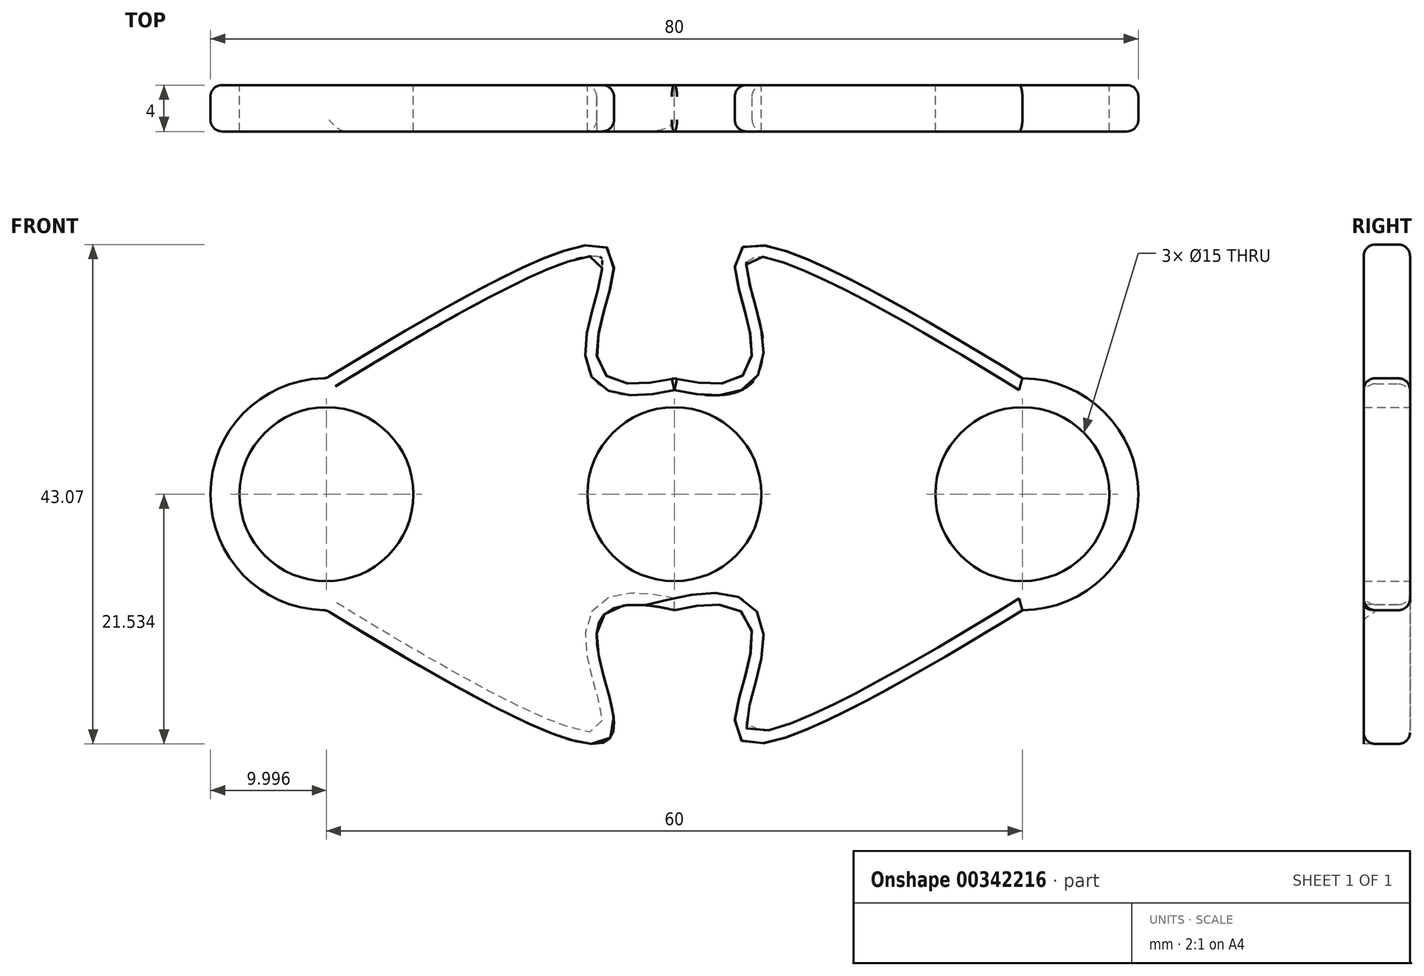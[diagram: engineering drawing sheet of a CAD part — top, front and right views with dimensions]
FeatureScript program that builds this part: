
annotation { "Feature Type Name" : "Feature", "Feature Type Description" : "" }
export const myFeature = defineFeature(function(context is Context, id is Id, definition is map)
    precondition{}
    {
        {
            var Q0;
            Q0=qCreatedBy(makeId("Front.planeOp"),FACE);
            var sketch = newSketch(context, id + "F0", { "sketchPlane" : qUnion([Q0])});
            skLineSegment(sketch, "E0.left", {"start": v(-32.53, 13.05) * mm, "end": v(-32.53, 13.05) * mm});
            skLineSegment(sketch, "E0.right", {"start": v(47.47, 13.05) * mm, "end": v(47.47, 13.05) * mm});
            skLineSegment(sketch, "E1", {"start": v(7.47, 23.05) * mm, "end": v(7.47, 3.05) * mm, "construction": true});
            skCircle(sketch, "E2", {"center": v(7.47, 13.05) * mm, "radius": 7.5 * mm});
            skLineSegment(sketch, "E3", {"start": v(27.47, 23.05) * mm, "end": v(27.47, 3.05) * mm, "construction": true});
            skLineSegment(sketch, "E4.MirrorCS", {"start": v(-12.53, 23.05) * mm, "end": v(-12.53, 3.05) * mm, "construction": true});
            skLineSegment(sketch, "E5", {"start": v(-32.53, 13.05) * mm, "end": v(47.47, 13.05) * mm, "construction": true});
            skCircle(sketch, "E6", {"center": v(37.47, 13.05) * mm, "radius": 7.5 * mm});
            skCircle(sketch, "E7.MirrorC", {"center": v(-22.53, 13.05) * mm, "radius": 7.5 * mm});
            skPoint(sketch, "E8.visualSharp", {"position": v(-32.53, 23.05) * mm});
            skArc(sketch, "E8.filletArc", {"start": v(-22.53, 23.05) * mm, "mid": v(-29.6, 20.13) * mm, "end": v(-32.53, 13.05) * mm});
            skPoint(sketch, "E9.visualSharp", {"position": v(-32.53, 3.05) * mm});
            skArc(sketch, "E9.filletArc", {"start": v(-32.53, 13.05) * mm, "mid": v(-29.6, 5.98) * mm, "end": v(-22.53, 3.05) * mm});
            skPoint(sketch, "E10.visualSharp", {"position": v(47.47, 23.05) * mm});
            skArc(sketch, "E10.filletArc", {"start": v(47.47, 13.05) * mm, "mid": v(44.54, 20.13) * mm, "end": v(37.47, 23.05) * mm});
            skPoint(sketch, "E11.visualSharp", {"position": v(47.47, 3.05) * mm});
            skArc(sketch, "E11.filletArc", {"start": v(37.47, 3.05) * mm, "mid": v(44.54, 5.98) * mm, "end": v(47.47, 13.05) * mm});
            skFitSpline(sketch, "E12", {"points": [v(-22.53, 23.05) * mm, v(7.47, 23.05) * mm], "startDerivative": vector(137.5, 84.56) * mm, "endDerivative": vector(60, 14.29) * mm});
            skFitSpline(sketch, "E13.MirrorCS", {"points": [v(37.47, 23.05) * mm, v(7.47, 23.05) * mm], "startDerivative": vector(-137.5, 84.56) * mm, "endDerivative": vector(-60, 14.29) * mm});
            skFitSpline(sketch, "E14.MirrorCS", {"points": [v(-22.53, 3.05) * mm, v(7.47, 3.05) * mm], "startDerivative": vector(137.5, -84.56) * mm, "endDerivative": vector(60, -14.29) * mm});
            skFitSpline(sketch, "E15.MirrorCS", {"points": [v(37.47, 3.05) * mm, v(7.47, 3.05) * mm], "startDerivative": vector(-137.5, -84.56) * mm, "endDerivative": vector(-60, -14.29) * mm});
            skSolve(sketch);
        }
        {
            var Q0;
            Q0=makeQuery(id+"F0.imprint","IMPRINT",FACE,{"disambiguationData":[TD([[makeQuery(id+"F0.imprint","IMPRINT",EDGE,{"derivedFrom":sQuery(id+"F0.wireOp",EDGE,"E2")}),-1.0]])]});
            extrude(context, id + "F1", {"entities" : qUnion([Q0]), "depth" : 4 * mm});
        }
        {
            var Q0;
            Q0=makeQuery(id+"F1.opExtrude","CAP_EDGE",EDGE,{"disambiguationData":[OSD([sQuery(id+"F0.wireOp",EDGE,"E12")])],"isStart":false});
            var Q1;
            Q1=makeQuery(id+"F1.opExtrude","CAP_EDGE",EDGE,{"disambiguationData":[OSD([sQuery(id+"F0.wireOp",EDGE,"E13.MirrorCS")])],"isStart":false});
            var Q2;
            Q2=makeQuery(id+"F1.opExtrude","CAP_EDGE",EDGE,{"disambiguationData":[OSD([sQuery(id+"F0.wireOp",EDGE,"E15.MirrorCS")])],"isStart":true});
            var Q3;
            Q3=makeQuery(id+"F1.opExtrude","CAP_EDGE",EDGE,{"disambiguationData":[OSD([sQuery(id+"F0.wireOp",EDGE,"E14.MirrorCS")])],"isStart":true});
            var Q4;
            Q4=makeQuery(id+"F1.opExtrude","CAP_EDGE",EDGE,{"disambiguationData":[OSD([sQuery(id+"F0.wireOp",EDGE,"E12")])],"isStart":true});
            var Q5;
            Q5=makeQuery(id+"F1.opExtrude","CAP_EDGE",EDGE,{"disambiguationData":[OSD([sQuery(id+"F0.wireOp",EDGE,"E8.filletArc"),sQuery(id+"F0.wireOp",EDGE,"E9.filletArc")])],"isStart":true});
            var Q6;
            Q6=makeQuery(id+"F1.opExtrude","SWEPT_FACE",FACE,{"disambiguationData":[OSD([sQuery(id+"F0.wireOp",EDGE,"E8.filletArc"),sQuery(id+"F0.wireOp",EDGE,"E9.filletArc")])]});
            var Q7;
            Q7=makeQuery(id+"F1.opExtrude","CAP_EDGE",EDGE,{"disambiguationData":[OSD([sQuery(id+"F0.wireOp",EDGE,"E13.MirrorCS")])],"isStart":true});
            var Q8;
            Q8=makeQuery(id+"F1.opExtrude","CAP_EDGE",EDGE,{"disambiguationData":[OSD([sQuery(id+"F0.wireOp",EDGE,"E10.filletArc"),sQuery(id+"F0.wireOp",EDGE,"E11.filletArc")])],"isStart":true});
            var Q9;
            Q9=makeQuery(id+"F1.opExtrude","CAP_EDGE",EDGE,{"disambiguationData":[OSD([sQuery(id+"F0.wireOp",EDGE,"E10.filletArc"),sQuery(id+"F0.wireOp",EDGE,"E11.filletArc")])],"isStart":false});
            var Q10;
            Q10=makeQuery(id+"F1.opExtrude","CAP_EDGE",EDGE,{"disambiguationData":[OSD([sQuery(id+"F0.wireOp",EDGE,"E15.MirrorCS")])],"isStart":false});
            fillet(context, id + "F2", {"entities" : qUnion([Q0, Q1, Q2, Q3, Q4, Q5, Q6, Q7, Q8, Q9, Q10]), "radius" : 1 * mm, "tangentPropagation" : true, "allowEdgeOverflow" : false});
        }
        {
            var Q0;
            Q0=makeQuery(id+"F2.opFillet","BLEND_EDGE",EDGE,{"blendedFrom":[makeQuery(id+"F1.opExtrude","CAP_EDGE",EDGE,{"disambiguationData":[OSD([sQuery(id+"F0.wireOp",EDGE,"E12")])],"isStart":false}),makeQuery(id+"F1.opExtrude","CAP_EDGE",EDGE,{"disambiguationData":[OSD([sQuery(id+"F0.wireOp",EDGE,"E13.MirrorCS")])],"isStart":false})],"blendedInto":[]});
            var Q1;
            Q1=makeQuery(id+"F2.opFillet","BLEND_EDGE",EDGE,{"blendedFrom":[makeQuery(id+"F1.opExtrude","CAP_EDGE",EDGE,{"disambiguationData":[OSD([sQuery(id+"F0.wireOp",EDGE,"E12")])],"isStart":true}),makeQuery(id+"F1.opExtrude","CAP_EDGE",EDGE,{"disambiguationData":[OSD([sQuery(id+"F0.wireOp",EDGE,"E13.MirrorCS")])],"isStart":true})],"blendedInto":[]});
            var Q2;
            Q2=makeQuery(id+"F2.opFillet","BLEND_EDGE",EDGE,{"blendedFrom":[makeQuery(id+"F1.opExtrude","CAP_EDGE",EDGE,{"disambiguationData":[OSD([sQuery(id+"F0.wireOp",EDGE,"E14.MirrorCS")])],"isStart":false}),makeQuery(id+"F1.opExtrude","CAP_EDGE",EDGE,{"disambiguationData":[OSD([sQuery(id+"F0.wireOp",EDGE,"E15.MirrorCS")])],"isStart":false})],"blendedInto":[]});
            fillet(context, id + "F3", {"entities" : qUnion([Q0, Q1, Q2]), "radius" : 1 * mm, "tangentPropagation" : true, "allowEdgeOverflow" : false});
        }
    });
